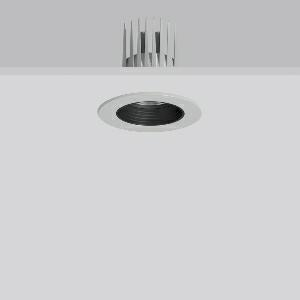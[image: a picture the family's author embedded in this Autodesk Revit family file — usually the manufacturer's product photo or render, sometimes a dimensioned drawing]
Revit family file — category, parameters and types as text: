
# Revit family: heledon_mini_e_901755_004_3_76_56ed
name_source: partatom
category: Lighting Fixtures
units: mm (PartAtom-declared; Revit-internal decimal feet)

## family parameters
Cut with Voids When Loaded = No
Host = Face
Light Source = No
Part Type = Normal
Room Calculation Point = No
Round Connector Dimension = Use Diameter
Shared = No

## types (1)
- HELEDON mini E (1 x LED Modul 935, 2800 lm, 3500)
    Apparent Load = 29 VA
    Approval mark = CE
    CIE Flux Codes = 95 100 100 100 100
    Color Rendering = 92
    Color Temperature = 3500
    Default Elevation = 1800 mm
    Description = Series: HELEDON mini
Round recessed downlight. Housing: die-cast aluminium, powder-coated. Black plastic ring and recessed LED to prevent glare from the side. Optical assembly with lens made of plastic (polycarbonate) for the best homogeneous light distribution - can be changed without tools. Best colour rendering index Ra>90. Suitable for Recessed ceiling mounting. Installation without tools thanks to spring fastening system. Including separate LED converter with connecting cable 600 mm.High quality converter without flickering and stroboscopic effect. Through-wiring box (5 pole) available as accessory. The following accessories can be mounted without use of tools: interchangeable lenses, decorative glasses, honeycomb louvre, clear and frosted diffusers, white interchangeable plastic ring. 
Colour: silver
Diameter: 124 mm
Height: 3 mm
Cut-out diameter: 114 mm
Recess height: 170 mm
Luminaire: recess height: 120 mm
Lamp: LED
Socket: without socket
Colour temperature: 3500K
Colour rendering index (CRI): 92
System power: 29 W
Rated luminous flux: 2800 lm
Luminous efficiency: 97 lm/W
Control gear: Converter, dimmable, DALI
Protection class: II
Type of protection: IP 20
    Height = 0 mm  [stored 0 ft]
    Lamp = 1 x LED Modul 935
    Lamp Light Flux = 2800 lm
    Lamp count = 1
    Length = 124 mm  [stored 0.406824 ft]
    Lifetime = 50000 h
    Luminous efficacy = 97 lm/W
    Manufacturer = RZB
    ModVariant = No
    Model = 901755.004.3.76
    Mounting Place = Ceiling
    Mounting Type = Recessed
    Number of Poles = 1
    OnlyDefault = Yes
    Power Factor = 1
    Product Name = HELEDON mini E
    Product group = Recessed downlights
    ProductGroupID = 402
    Protection Class = Protection class II
    Protection Degree = IP 20
    RLX_Detail_Level = 1
    RLX_Emergency_Light_Flux = 0 lm
    RLX_Emergency_Type = 0
    RLX_Emergency_Type_DB = No
    RlxData = <blob elided: 135805 chars, md5=b9d4f418>
    Socket = socket
    Standby Power = 0 W
    System Light Flux = 2800 lm
    System Power = 29 W
    Type Comments = Product without accessories
    Type Image = 901656.004.jpg
    URL = http://relux.com
    VarID = ---
    Voltage = 230 V
    Voltage Range = 220-240 V
    Weight = 0.00 kg
    Width = 0 mm  [stored 0 ft]

note: [stored X ft] marks values corroborated as IEEE doubles in the binary element streams (Revit-internal decimal feet)

## geometry (parser evidence)
native form markers: Blend x4, Sweep x9
no freeform markers — native parametric forms only
